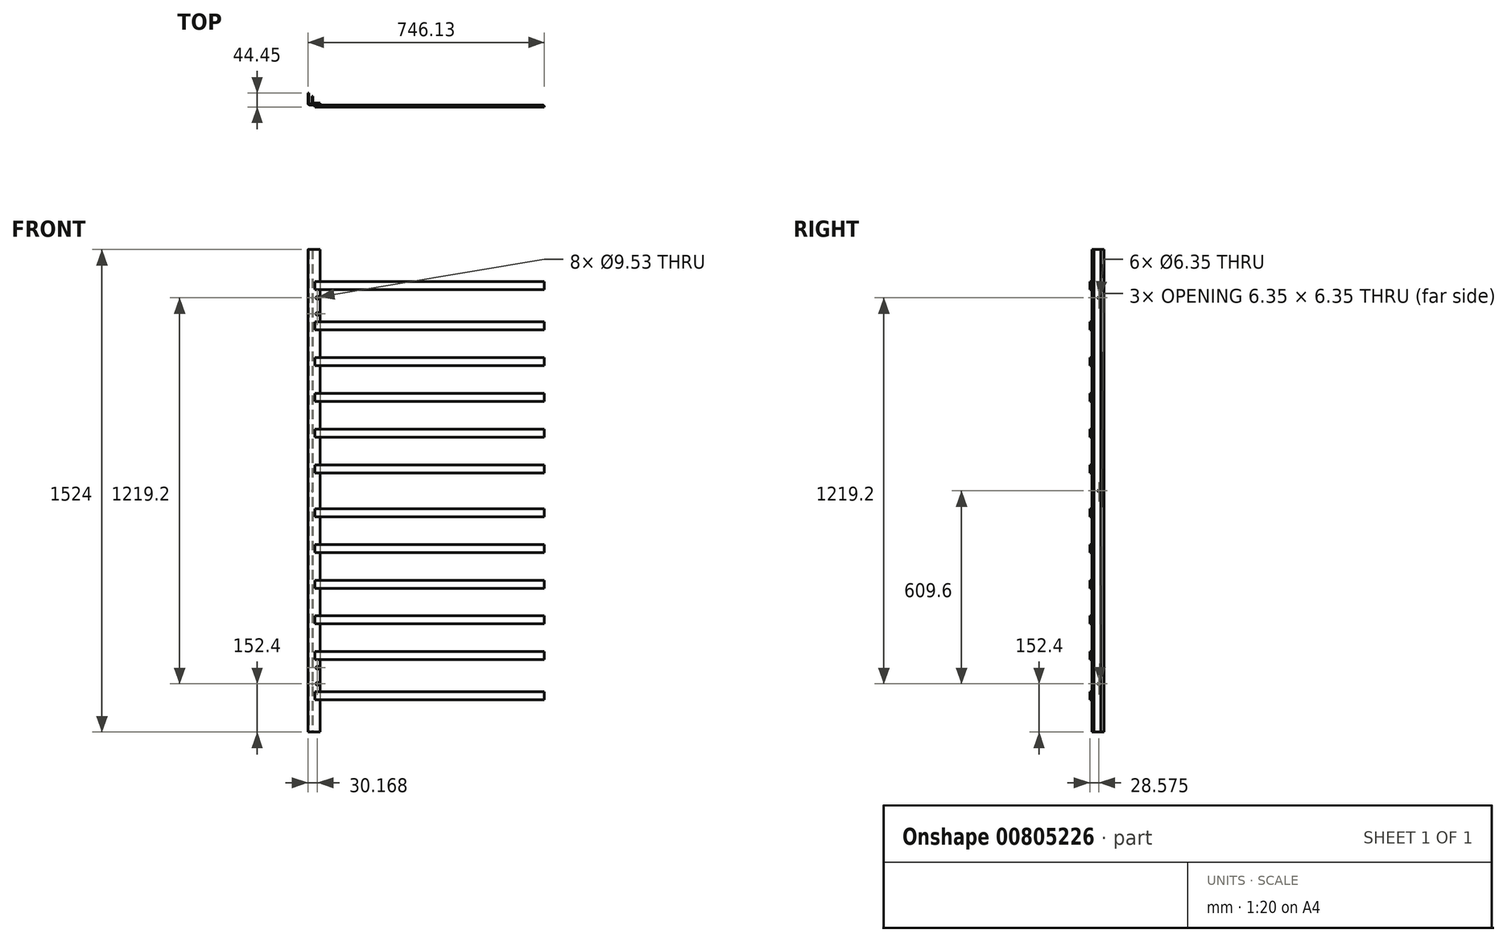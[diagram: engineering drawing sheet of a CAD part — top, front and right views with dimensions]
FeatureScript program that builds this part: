
annotation { "Feature Type Name" : "Feature", "Feature Type Description" : "" }
export const myFeature = defineFeature(function(context is Context, id is Id, definition is map)
    precondition{}
    {
        {
            var Q0;
            Q0=qCreatedBy(makeId("Top.planeOp"),FACE);
            var sketch = newSketch(context, id + "F0", { "sketchPlane" : qUnion([Q0])});
            skLineSegment(sketch, "E0", {"start": v(-384.18, 0) * mm, "end": v(-384.18, -31.75) * mm});
            skLineSegment(sketch, "E1", {"start": v(-377.83, -38.1) * mm, "end": v(-346.08, -38.1) * mm});
            skLineSegment(sketch, "E2", {"start": v(-346.08, -38.1) * mm, "end": v(-346.08, -34.93) * mm});
            skLineSegment(sketch, "E3", {"start": v(-346.08, -34.93) * mm, "end": v(-374.65, -34.93) * mm});
            skLineSegment(sketch, "E4", {"start": v(-381, -28.58) * mm, "end": v(-381, 0) * mm});
            skLineSegment(sketch, "E5", {"start": v(-381, 0) * mm, "end": v(-384.17, 0) * mm});
            skPoint(sketch, "E6.visualSharp", {"position": v(-381, -34.93) * mm});
            skArc(sketch, "E6.filletArc", {"start": v(-381, -28.58) * mm, "mid": v(-379.14, -33.07) * mm, "end": v(-374.65, -34.93) * mm});
            skPoint(sketch, "E7.visualSharp", {"position": v(-384.18, -38.1) * mm});
            skArc(sketch, "E7.filletArc", {"start": v(-384.18, -31.75) * mm, "mid": v(-382.32, -36.24) * mm, "end": v(-377.83, -38.1) * mm});
            skLineSegment(sketch, "E8", {"start": v(-371.48, -9.53) * mm, "end": v(-371.48, -28.58) * mm});
            skLineSegment(sketch, "E9", {"start": v(-365.12, -34.93) * mm, "end": v(-346.08, -34.93) * mm});
            skLineSegment(sketch, "E10", {"start": v(-346.07, -34.93) * mm, "end": v(-346.07, -31.75) * mm});
            skLineSegment(sketch, "E11", {"start": v(-346.08, -31.75) * mm, "end": v(-361.95, -31.75) * mm});
            skLineSegment(sketch, "E12", {"start": v(-368.3, -25.4) * mm, "end": v(-368.3, -9.53) * mm});
            skLineSegment(sketch, "E13", {"start": v(-368.3, -9.53) * mm, "end": v(-371.48, -9.53) * mm});
            skPoint(sketch, "E14.visualSharp", {"position": v(-368.3, -31.75) * mm});
            skArc(sketch, "E14.filletArc", {"start": v(-368.3, -25.4) * mm, "mid": v(-366.44, -29.9) * mm, "end": v(-361.95, -31.75) * mm});
            skPoint(sketch, "E15.visualSharp", {"position": v(-371.48, -34.93) * mm});
            skArc(sketch, "E15.filletArc", {"start": v(-371.48, -28.58) * mm, "mid": v(-369.62, -33.07) * mm, "end": v(-365.12, -34.93) * mm});
            skLineSegment(sketch, "E16", {"start": v(0, 129.47) * mm, "end": v(0, -160.72) * mm, "construction": true});
            skArc(sketch, "E17.MirrorCS", {"start": v(371.48, -28.58) * mm, "mid": v(369.62, -33.07) * mm, "end": v(365.12, -34.93) * mm});
            skArc(sketch, "E18.MirrorCS", {"start": v(368.3, -25.4) * mm, "mid": v(366.44, -29.9) * mm, "end": v(361.95, -31.75) * mm});
            skArc(sketch, "E19.MirrorCS", {"start": v(384.18, -31.75) * mm, "mid": v(382.32, -36.24) * mm, "end": v(377.83, -38.1) * mm});
            skArc(sketch, "E20.MirrorCS", {"start": v(381, -28.58) * mm, "mid": v(379.14, -33.07) * mm, "end": v(374.65, -34.93) * mm});
            skLineSegment(sketch, "E21.MirrorCS", {"start": v(346.07, -34.93) * mm, "end": v(346.07, -31.75) * mm});
            skLineSegment(sketch, "E22.MirrorCS", {"start": v(346.08, -38.1) * mm, "end": v(346.08, -34.93) * mm});
            skLineSegment(sketch, "E23.MirrorCS", {"start": v(346.08, -34.93) * mm, "end": v(374.65, -34.93) * mm});
            skLineSegment(sketch, "E24.MirrorCS", {"start": v(368.3, -25.4) * mm, "end": v(368.3, -9.53) * mm});
            skLineSegment(sketch, "E25.MirrorCS", {"start": v(346.08, -31.75) * mm, "end": v(361.95, -31.75) * mm});
            skLineSegment(sketch, "E26.MirrorCS", {"start": v(368.3, -9.53) * mm, "end": v(371.48, -9.53) * mm});
            skLineSegment(sketch, "E27.MirrorCS", {"start": v(377.83, -38.1) * mm, "end": v(346.08, -38.1) * mm});
            skLineSegment(sketch, "E28.MirrorCS", {"start": v(365.12, -34.93) * mm, "end": v(346.08, -34.93) * mm});
            skLineSegment(sketch, "E29.MirrorCS", {"start": v(371.48, -9.53) * mm, "end": v(371.48, -28.58) * mm});
            skLineSegment(sketch, "E30.MirrorCS", {"start": v(381, 0) * mm, "end": v(384.17, 0) * mm});
            skLineSegment(sketch, "E31.MirrorCS", {"start": v(381, -28.58) * mm, "end": v(381, 0) * mm});
            skLineSegment(sketch, "E32.MirrorCS", {"start": v(384.18, 0) * mm, "end": v(384.18, -31.75) * mm});
            skPoint(sketch, "E33.MirrorP", {"position": v(368.3, -31.75) * mm});
            skPoint(sketch, "E34.MirrorP", {"position": v(371.48, -34.93) * mm});
            skPoint(sketch, "E35.MirrorP", {"position": v(384.18, -38.1) * mm});
            skPoint(sketch, "E36.MirrorP", {"position": v(381, -34.93) * mm});
            skSolve(sketch);
        }
        {
            var Q0;
            Q0=makeQuery(id+"F0.imprint","IMPRINT",FACE,{"disambiguationData":[TD([[makeQuery(id+"F0.imprint","IMPRINT",EDGE,{"derivedFrom":sQuery(id+"F0.wireOp",EDGE,"E0")}),1.0]])]});
            var Q1;
            Q1=makeQuery(id+"F0.imprint","IMPRINT",FACE,{"disambiguationData":[TD([[makeQuery(id+"F0.imprint","IMPRINT",EDGE,{"derivedFrom":sQuery(id+"F0.wireOp",EDGE,"E19.MirrorCS")}),-1.0]])]});
            extrude(context, id + "F1", {"entities" : qUnion([Q0, Q1]), "depth" : 1524 * mm, "offsetDistance" : 25.4 * mm});
        }
        {
            var Q0;
            {var subQ2=sQuery(id+"F0.wireOp",EDGE,"E17.MirrorCS");Q0=makeQuery(id+"F0.imprint","IMPRINT",FACE,{"disambiguationData":[TD([[makeQuery(id+"F0.imprint","IMPRINT",EDGE,{"derivedFrom":subQ2}),-1.0]])]});}
            var Q1;
            Q1=makeQuery(id+"F0.imprint","IMPRINT",FACE,{"disambiguationData":[TD([[makeQuery(id+"F0.imprint","IMPRINT",EDGE,{"derivedFrom":sQuery(id+"F0.wireOp",EDGE,"E8")}),1.0]])]});
            extrude(context, id + "F2", {"entities" : qUnion([Q0, Q1]), "depth" : 1524 * mm, "offsetDistance" : 25.4 * mm});
        }
        {
            var Q0;
            Q0=qCreatedBy(makeId("Right.planeOp"),FACE);
            var sketch = newSketch(context, id + "F3", { "sketchPlane" : qUnion([Q0])});
            skLineSegment(sketch, "E37.0", {"start": v(0, 0) * mm, "end": v(-31.75, 0) * mm, "construction": true});
            skCircle(sketch, "E38", {"center": v(-15.88, 152.4) * mm, "radius": 3.18 * mm});
            skPoint(sketch, "E38.centerSnap0", {"position": v(-15.88, 0) * mm});
            skCircle(sketch, "E39", {"center": v(-15.88, 762) * mm, "radius": 3.17 * mm});
            skCircle(sketch, "E40", {"center": v(-15.88, 1371.6) * mm, "radius": 3.17 * mm});
            skSolve(sketch);
        }
        {
            var Q0;
            Q0 = qSketchRegion(id + "F3", true);
            extrude(context, id + "F4", {"entities" : qUnion([Q0]), "operationType" : NewBodyOperationType.REMOVE, "endBound" : BoundingType.THROUGH_ALL, "oppositeDirection" : true, "depth" : 25.4 * mm, "offsetDistance" : 25.4 * mm, "hasSecondDirection" : true, "secondDirectionBound" : SecondDirectionBoundingType.THROUGH_ALL, "secondDirectionOppositeDirection" : false, "secondDirectionDepth" : 25.4 * mm});
        }
        {
            var Q0;
            Q0=qCreatedBy(makeId("Front.planeOp"),FACE);
            var sketch = newSketch(context, id + "F5", { "sketchPlane" : qUnion([Q0])});
            skLineSegment(sketch, "E41.0", {"start": v(-346.08, 0) * mm, "end": v(-361.95, 0) * mm, "construction": true});
            skCircle(sketch, "E42", {"center": v(-354.01, 152.4) * mm, "radius": 3.18 * mm});
            skPoint(sketch, "E42.centerSnap0", {"position": v(-354.01, 0) * mm});
            skCircle(sketch, "E43", {"center": v(-354.01, 203.2) * mm, "radius": 3.18 * mm});
            skCircle(sketch, "E44", {"center": v(-354.01, 1320.8) * mm, "radius": 3.18 * mm});
            skCircle(sketch, "E45", {"center": v(-354.01, 1371.6) * mm, "radius": 3.18 * mm});
            skLineSegment(sketch, "E46", {"start": v(0, -156.86) * mm, "end": v(0, 289.59) * mm, "construction": true});
            skCircle(sketch, "E47.MirrorC", {"center": v(354.01, 152.4) * mm, "radius": 3.18 * mm});
            skCircle(sketch, "E48.MirrorC", {"center": v(354.01, 203.2) * mm, "radius": 3.18 * mm});
            skCircle(sketch, "E49.MirrorC", {"center": v(354.01, 1371.6) * mm, "radius": 3.18 * mm});
            skCircle(sketch, "E50.MirrorC", {"center": v(354.01, 1320.8) * mm, "radius": 3.18 * mm});
            skSolve(sketch);
        }
        {
            var Q0;
            Q0=qCreatedBy(makeId("Front.planeOp"),FACE);
            var sketch = newSketch(context, id + "F6", { "sketchPlane" : qUnion([Q0])});
            skCircle(sketch, "E51.0", {"center": v(-354.01, 1371.6) * mm, "radius": 4.76 * mm});
            skCircle(sketch, "E52.0", {"center": v(-354.01, 1320.8) * mm, "radius": 4.76 * mm});
            skCircle(sketch, "E53.0", {"center": v(-354.01, 203.2) * mm, "radius": 4.76 * mm});
            skCircle(sketch, "E54.0", {"center": v(-354.01, 152.4) * mm, "radius": 4.76 * mm});
            skCircle(sketch, "E55.0", {"center": v(354.01, 152.4) * mm, "radius": 4.76 * mm});
            skCircle(sketch, "E56.0", {"center": v(354.01, 203.2) * mm, "radius": 4.76 * mm});
            skCircle(sketch, "E57.0", {"center": v(354.01, 1371.6) * mm, "radius": 4.76 * mm});
            skCircle(sketch, "E58.0", {"center": v(354.01, 1320.8) * mm, "radius": 4.76 * mm});
            skSolve(sketch);
        }
        {
            var Q0;
            Q0 = qSketchRegion(id + "F5", true);
            extrude(context, id + "F7", {"entities" : qUnion([Q0]), "operationType" : NewBodyOperationType.REMOVE, "endBound" : BoundingType.THROUGH_ALL, "depth" : 25.4 * mm, "offsetDistance" : 25.4 * mm});
        }
        {
            var Q0;
            Q0 = qSketchRegion(id + "F6", true);
            extrude(context, id + "F8", {"entities" : qUnion([Q0]), "operationType" : NewBodyOperationType.REMOVE, "endBound" : BoundingType.THROUGH_ALL, "depth" : 25.4 * mm, "offsetDistance" : 25.4 * mm});
        }
        {
            var Q0;
            Q0=makeQuery(id+"F1.opExtrude","SWEPT_FACE",FACE,{"disambiguationData":[OSD([sQuery(id+"F0.wireOp",EDGE,"E1")])]});
            var sketch = newSketch(context, id + "F9", { "sketchPlane" : qUnion([Q0])});
            skLineSegment(sketch, "E59.0", {"start": v(-377.83, 1524) * mm, "end": v(-346.08, 1524) * mm, "construction": true});
            skLineSegment(sketch, "E60.0", {"start": v(377.83, 1524) * mm, "end": v(346.08, 1524) * mm, "construction": true});
            skPoint(sketch, "E61.firstSnap0", {"position": v(-361.95, 1524) * mm});
            skPoint(sketch, "E61.oppositeSnap0", {"position": v(361.95, 1524) * mm});
            skLineSegment(sketch, "E61.bottom", {"start": v(-361.95, 1422.4) * mm, "end": v(361.95, 1422.4) * mm});
            skLineSegment(sketch, "E61.top", {"start": v(-361.95, 1397) * mm, "end": v(361.95, 1397) * mm});
            skLineSegment(sketch, "E61.left", {"start": v(-361.95, 1422.4) * mm, "end": v(-361.95, 1397) * mm});
            skLineSegment(sketch, "E61.right", {"start": v(361.95, 1422.4) * mm, "end": v(361.95, 1397) * mm});
            skLineSegment(sketch, "E62.direction1", {"start": v(-361.95, 1397) * mm, "end": v(-534.38, 1369.84) * mm, "construction": true});
            skLineSegment(sketch, "E62.direction2", {"start": v(-361.95, 1397) * mm, "end": v(-361.95, 1270) * mm, "construction": true});
            skLineSegment(sketch, "E63", {"start": v(-346.08, 762) * mm, "end": v(346.08, 762) * mm, "construction": true});
            skLineSegment(sketch, "E64.0.0.1", {"start": v(-361.95, 1295.4) * mm, "end": v(-361.95, 1270) * mm});
            skLineSegment(sketch, "E64.3.0.1", {"start": v(-361.95, 1295.4) * mm, "end": v(361.95, 1295.4) * mm});
            skLineSegment(sketch, "E64.6.0.1", {"start": v(-361.95, 1270) * mm, "end": v(361.95, 1270) * mm});
            skLineSegment(sketch, "E64.9.0.1", {"start": v(361.95, 1295.4) * mm, "end": v(361.95, 1270) * mm});
            skLineSegment(sketch, "E65.0.1.0", {"start": v(-361.95, 1182.51) * mm, "end": v(-361.95, 1157.11) * mm});
            skLineSegment(sketch, "E65.0.1.1", {"start": v(-361.95, 1157.11) * mm, "end": v(361.95, 1157.11) * mm});
            skLineSegment(sketch, "E65.0.1.2", {"start": v(-361.95, 1182.51) * mm, "end": v(361.95, 1182.51) * mm});
            skLineSegment(sketch, "E65.0.1.3", {"start": v(361.95, 1182.51) * mm, "end": v(361.95, 1157.11) * mm});
            skLineSegment(sketch, "E65.0.2.0", {"start": v(-361.95, 1069.62) * mm, "end": v(-361.95, 1044.22) * mm});
            skLineSegment(sketch, "E65.0.2.1", {"start": v(-361.95, 1044.22) * mm, "end": v(361.95, 1044.22) * mm});
            skLineSegment(sketch, "E65.0.2.2", {"start": v(-361.95, 1069.62) * mm, "end": v(361.95, 1069.62) * mm});
            skLineSegment(sketch, "E65.0.2.3", {"start": v(361.95, 1069.62) * mm, "end": v(361.95, 1044.22) * mm});
            skLineSegment(sketch, "E65.0.3.0", {"start": v(-361.95, 956.73) * mm, "end": v(-361.95, 931.33) * mm});
            skLineSegment(sketch, "E65.0.3.1", {"start": v(-361.95, 931.33) * mm, "end": v(361.95, 931.33) * mm});
            skLineSegment(sketch, "E65.0.3.2", {"start": v(-361.95, 956.73) * mm, "end": v(361.95, 956.73) * mm});
            skLineSegment(sketch, "E65.0.3.3", {"start": v(361.95, 956.73) * mm, "end": v(361.95, 931.33) * mm});
            skLineSegment(sketch, "E65.direction1", {"start": v(-361.95, 1270) * mm, "end": v(-541.89, 1250.7) * mm, "construction": true});
            skLineSegment(sketch, "E65.direction2", {"start": v(-361.95, 1270) * mm, "end": v(-361.95, 1157.11) * mm, "construction": true});
            skLineSegment(sketch, "E66.0.0.4", {"start": v(-361.95, 843.84) * mm, "end": v(-361.95, 818.44) * mm});
            skLineSegment(sketch, "E66.3.0.4", {"start": v(-361.95, 818.44) * mm, "end": v(361.95, 818.44) * mm});
            skLineSegment(sketch, "E66.6.0.4", {"start": v(-361.95, 843.84) * mm, "end": v(361.95, 843.84) * mm});
            skLineSegment(sketch, "E66.9.0.4", {"start": v(361.95, 843.84) * mm, "end": v(361.95, 818.44) * mm});
            skLineSegment(sketch, "E67.MirrorCS", {"start": v(361.95, 454.38) * mm, "end": v(361.95, 479.78) * mm});
            skLineSegment(sketch, "E68.MirrorCS", {"start": v(361.95, 567.27) * mm, "end": v(361.95, 592.67) * mm});
            skLineSegment(sketch, "E69.MirrorCS", {"start": v(361.95, 101.6) * mm, "end": v(361.95, 127) * mm});
            skLineSegment(sketch, "E70.MirrorCS", {"start": v(361.95, 680.16) * mm, "end": v(361.95, 705.56) * mm});
            skLineSegment(sketch, "E71.MirrorCS", {"start": v(361.95, 228.6) * mm, "end": v(361.95, 254) * mm});
            skLineSegment(sketch, "E72.MirrorCS", {"start": v(361.95, 341.49) * mm, "end": v(361.95, 366.89) * mm});
            skLineSegment(sketch, "E73.MirrorCS", {"start": v(-361.95, 567.27) * mm, "end": v(361.95, 567.27) * mm});
            skLineSegment(sketch, "E74.MirrorCS", {"start": v(-361.95, 680.16) * mm, "end": v(361.95, 680.16) * mm});
            skLineSegment(sketch, "E75.MirrorCS", {"start": v(-361.95, 592.67) * mm, "end": v(361.95, 592.67) * mm});
            skLineSegment(sketch, "E76.MirrorCS", {"start": v(-361.95, 127) * mm, "end": v(361.95, 127) * mm});
            skLineSegment(sketch, "E77.MirrorCS", {"start": v(-361.95, 228.6) * mm, "end": v(361.95, 228.6) * mm});
            skLineSegment(sketch, "E78.MirrorCS", {"start": v(-361.95, 705.56) * mm, "end": v(361.95, 705.56) * mm});
            skLineSegment(sketch, "E79.MirrorCS", {"start": v(-361.95, 454.38) * mm, "end": v(361.95, 454.38) * mm});
            skLineSegment(sketch, "E80.MirrorCS", {"start": v(-361.95, 254) * mm, "end": v(361.95, 254) * mm});
            skLineSegment(sketch, "E81.MirrorCS", {"start": v(-361.95, 101.6) * mm, "end": v(361.95, 101.6) * mm});
            skLineSegment(sketch, "E82.MirrorCS", {"start": v(-361.95, 341.49) * mm, "end": v(361.95, 341.49) * mm});
            skLineSegment(sketch, "E83.MirrorCS", {"start": v(-361.95, 366.89) * mm, "end": v(361.95, 366.89) * mm});
            skLineSegment(sketch, "E84.MirrorCS", {"start": v(-361.95, 479.78) * mm, "end": v(361.95, 479.78) * mm});
            skLineSegment(sketch, "E85.MirrorCS", {"start": v(-361.95, 101.6) * mm, "end": v(-361.95, 127) * mm});
            skLineSegment(sketch, "E86.MirrorCS", {"start": v(-361.95, 228.6) * mm, "end": v(-361.95, 254) * mm});
            skLineSegment(sketch, "E87.MirrorCS", {"start": v(-361.95, 341.49) * mm, "end": v(-361.95, 366.89) * mm});
            skLineSegment(sketch, "E88.MirrorCS", {"start": v(-361.95, 454.38) * mm, "end": v(-361.95, 479.78) * mm});
            skLineSegment(sketch, "E89.MirrorCS", {"start": v(-361.95, 567.27) * mm, "end": v(-361.95, 592.67) * mm});
            skLineSegment(sketch, "E90.MirrorCS", {"start": v(-361.95, 680.16) * mm, "end": v(-361.95, 705.56) * mm});
            skSolve(sketch);
        }
        {
            var Q0;
            Q0 = qSketchRegion(id + "F9", true);
            extrude(context, id + "F10", {"entities" : qUnion([Q0]), "depth" : 6.35 * mm, "offsetDistance" : 25.4 * mm});
        }
        {
            var Q0;
            Q0=makeQuery(id+"F10.opExtrude","CAP_EDGE",EDGE,{"disambiguationData":[OSD([sQuery(id+"F9.wireOp",EDGE,"E61.right")])],"isStart":true});
            var Q1;
            Q1=makeQuery(id+"F10.opExtrude","CAP_EDGE",EDGE,{"disambiguationData":[OSD([sQuery(id+"F9.wireOp",EDGE,"E64.9.0.1")])],"isStart":true});
            var Q2;
            Q2=makeQuery(id+"F10.opExtrude","CAP_EDGE",EDGE,{"disambiguationData":[OSD([sQuery(id+"F9.wireOp",EDGE,"E65.0.1.3")])],"isStart":true});
            var Q3;
            Q3=makeQuery(id+"F10.opExtrude","CAP_EDGE",EDGE,{"disambiguationData":[OSD([sQuery(id+"F9.wireOp",EDGE,"E65.0.2.3")])],"isStart":true});
            var Q4;
            Q4=makeQuery(id+"F10.opExtrude","CAP_EDGE",EDGE,{"disambiguationData":[OSD([sQuery(id+"F9.wireOp",EDGE,"E65.0.3.3")])],"isStart":true});
            var Q5;
            Q5=makeQuery(id+"F10.opExtrude","CAP_EDGE",EDGE,{"disambiguationData":[OSD([sQuery(id+"F9.wireOp",EDGE,"E66.9.0.4")])],"isStart":true});
            var Q6;
            Q6=makeQuery(id+"F10.opExtrude","CAP_EDGE",EDGE,{"disambiguationData":[OSD([sQuery(id+"F9.wireOp",EDGE,"E70.MirrorCS")])],"isStart":true});
            var Q7;
            Q7=makeQuery(id+"F10.opExtrude","CAP_EDGE",EDGE,{"disambiguationData":[OSD([sQuery(id+"F9.wireOp",EDGE,"E68.MirrorCS")])],"isStart":true});
            var Q8;
            Q8=makeQuery(id+"F10.opExtrude","CAP_EDGE",EDGE,{"disambiguationData":[OSD([sQuery(id+"F9.wireOp",EDGE,"E67.MirrorCS")])],"isStart":true});
            var Q9;
            Q9=makeQuery(id+"F10.opExtrude","CAP_EDGE",EDGE,{"disambiguationData":[OSD([sQuery(id+"F9.wireOp",EDGE,"E72.MirrorCS")])],"isStart":true});
            var Q10;
            Q10=makeQuery(id+"F10.opExtrude","CAP_EDGE",EDGE,{"disambiguationData":[OSD([sQuery(id+"F9.wireOp",EDGE,"E71.MirrorCS")])],"isStart":true});
            var Q11;
            Q11=makeQuery(id+"F10.opExtrude","CAP_EDGE",EDGE,{"disambiguationData":[OSD([sQuery(id+"F9.wireOp",EDGE,"E69.MirrorCS")])],"isStart":true});
            var Q12;
            Q12=makeQuery(id+"F10.opExtrude","CAP_EDGE",EDGE,{"disambiguationData":[OSD([sQuery(id+"F9.wireOp",EDGE,"E85.MirrorCS")])],"isStart":true});
            var Q13;
            Q13=makeQuery(id+"F10.opExtrude","CAP_EDGE",EDGE,{"disambiguationData":[OSD([sQuery(id+"F9.wireOp",EDGE,"E86.MirrorCS")])],"isStart":true});
            var Q14;
            Q14=makeQuery(id+"F10.opExtrude","CAP_EDGE",EDGE,{"disambiguationData":[OSD([sQuery(id+"F9.wireOp",EDGE,"E87.MirrorCS")])],"isStart":true});
            var Q15;
            Q15=makeQuery(id+"F10.opExtrude","CAP_EDGE",EDGE,{"disambiguationData":[OSD([sQuery(id+"F9.wireOp",EDGE,"E88.MirrorCS")])],"isStart":true});
            var Q16;
            Q16=makeQuery(id+"F10.opExtrude","CAP_EDGE",EDGE,{"disambiguationData":[OSD([sQuery(id+"F9.wireOp",EDGE,"E89.MirrorCS")])],"isStart":true});
            var Q17;
            Q17=makeQuery(id+"F10.opExtrude","CAP_EDGE",EDGE,{"disambiguationData":[OSD([sQuery(id+"F9.wireOp",EDGE,"E90.MirrorCS")])],"isStart":true});
            var Q18;
            Q18=makeQuery(id+"F10.opExtrude","CAP_EDGE",EDGE,{"disambiguationData":[OSD([sQuery(id+"F9.wireOp",EDGE,"E66.0.0.4")])],"isStart":true});
            var Q19;
            Q19=makeQuery(id+"F10.opExtrude","CAP_EDGE",EDGE,{"disambiguationData":[OSD([sQuery(id+"F9.wireOp",EDGE,"E65.0.3.0")])],"isStart":true});
            var Q20;
            Q20=makeQuery(id+"F10.opExtrude","CAP_EDGE",EDGE,{"disambiguationData":[OSD([sQuery(id+"F9.wireOp",EDGE,"E65.0.2.0")])],"isStart":true});
            var Q21;
            Q21=makeQuery(id+"F10.opExtrude","CAP_EDGE",EDGE,{"disambiguationData":[OSD([sQuery(id+"F9.wireOp",EDGE,"E65.0.1.0")])],"isStart":true});
            var Q22;
            Q22=makeQuery(id+"F10.opExtrude","CAP_EDGE",EDGE,{"disambiguationData":[OSD([sQuery(id+"F9.wireOp",EDGE,"E64.0.0.1")])],"isStart":true});
            var Q23;
            Q23=makeQuery(id+"F10.opExtrude","CAP_EDGE",EDGE,{"disambiguationData":[OSD([sQuery(id+"F9.wireOp",EDGE,"E61.left")])],"isStart":true});
            fillet(context, id + "F11", {"entities" : qUnion([Q0, Q1, Q2, Q3, Q4, Q5, Q6, Q7, Q8, Q9, Q10, Q11, Q12, Q13, Q14, Q15, Q16, Q17, Q18, Q19, Q20, Q21, Q22, Q23]), "radius" : 5.08 * mm, "tangentPropagation" : true, "allowEdgeOverflow" : false});
        }
    });
